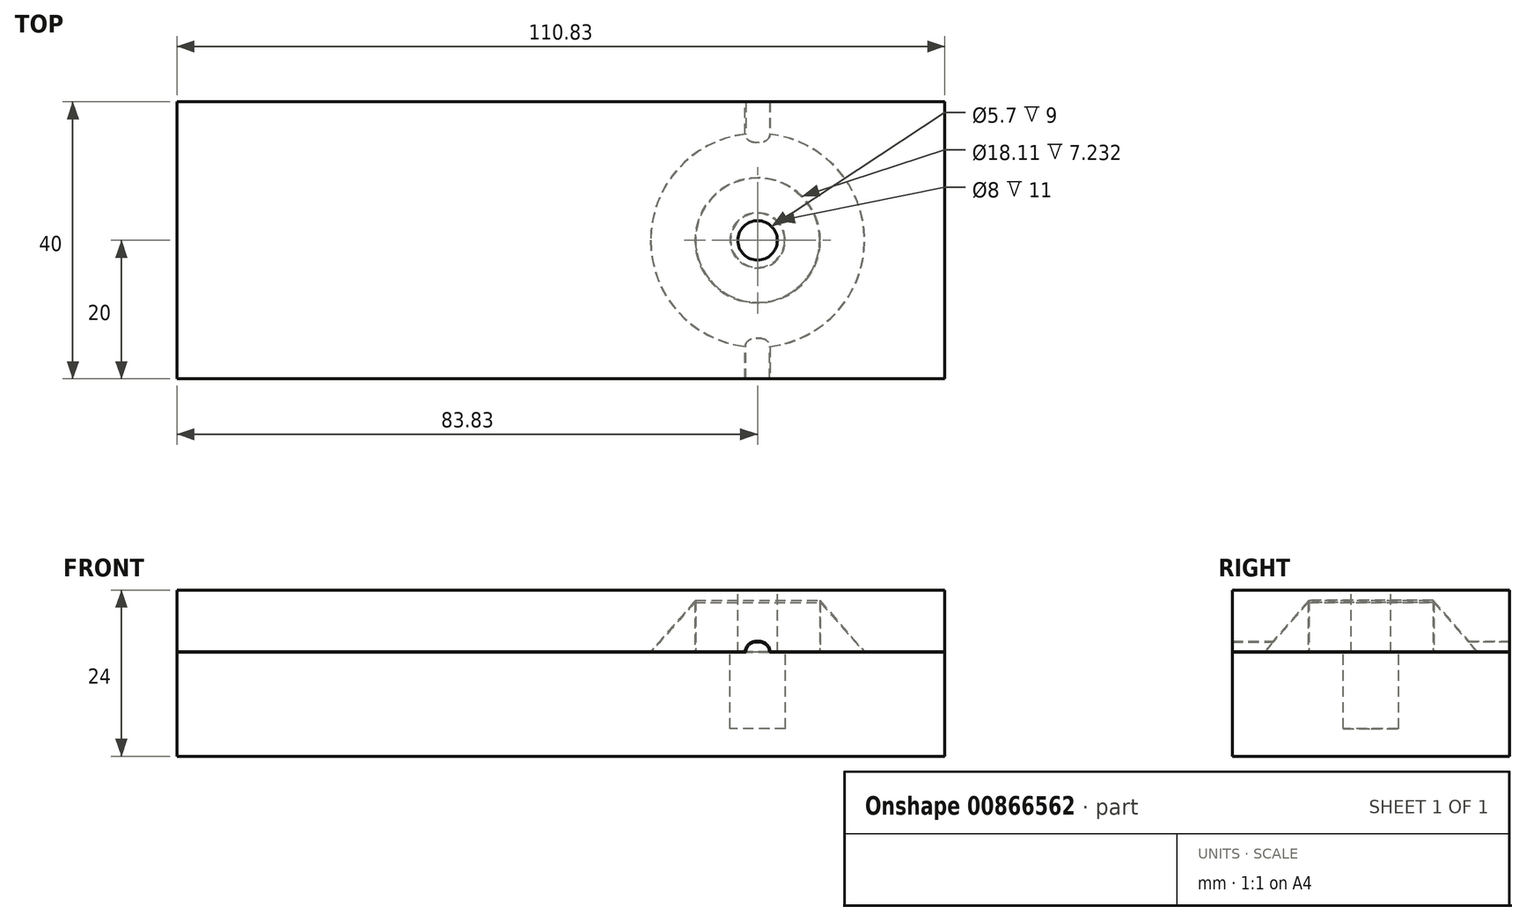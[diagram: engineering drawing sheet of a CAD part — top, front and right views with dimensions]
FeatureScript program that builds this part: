
annotation { "Feature Type Name" : "Feature", "Feature Type Description" : "" }
export const myFeature = defineFeature(function(context is Context, id is Id, definition is map)
    precondition{}
    {
        {
            var Q0;
            Q0=qCreatedBy(makeId("Top.planeOp"),FACE);
            var sketch = newSketch(context, id + "F0", { "sketchPlane" : qUnion([Q0])});
            skLineSegment(sketch, "E0.bottom", {"start": v(27, -20) * mm, "end": v(-83.83, -20) * mm});
            skLineSegment(sketch, "E0.top", {"start": v(27, 20) * mm, "end": v(-83.83, 20) * mm});
            skLineSegment(sketch, "E0.left", {"start": v(27, -20) * mm, "end": v(27, 20) * mm});
            skLineSegment(sketch, "E0.right", {"start": v(-83.83, -20) * mm, "end": v(-83.83, 20) * mm});
            skSolve(sketch);
        }
        {
            var Q0;
            Q0=makeQuery(id+"F0.imprint","IMPRINT",FACE,{"disambiguationData":[TD([[makeQuery(id+"F0.imprint","IMPRINT",EDGE,{"derivedFrom":sQuery(id+"F0.wireOp",EDGE,"E0.bottom")}),-1.0]])]});
            extrude(context, id + "F1", {"entities" : qUnion([Q0]), "depth" : 15 * mm, "offsetDistance" : 25 * mm});
        }
        {
            var Q0;
            Q0=makeQuery(id+"F1.opExtrude","CAP_FACE",FACE,{"disambiguationData":[OSD([sQuery(id+"F0.wireOp",EDGE,"E0.bottom"),sQuery(id+"F0.wireOp",EDGE,"E0.top"),sQuery(id+"F0.wireOp",EDGE,"E0.left"),sQuery(id+"F0.wireOp",EDGE,"E0.right")])],"isStart":false});
            var sketch = newSketch(context, id + "F2", { "sketchPlane" : qUnion([Q0])});
            skCircle(sketch, "E1", {"center": v(0, 0) * mm, "radius": 4 * mm});
            skSolve(sketch);
        }
        {
            var Q0;
            Q0=qCreatedBy(makeId("Right.planeOp"),FACE);
            var sketch = newSketch(context, id + "F3", { "sketchPlane" : qUnion([Q0])});
            skLineSegment(sketch, "E2", {"start": v(9.06, 15) * mm, "end": v(9.06, 22.23) * mm});
            skLineSegment(sketch, "E3", {"start": v(9.06, 22.23) * mm, "end": v(15.4, 15) * mm});
            skLineSegment(sketch, "E4", {"start": v(15.4, 15) * mm, "end": v(9.06, 15) * mm});
            skSolve(sketch);
        }
        {
            var Q0;
            Q0=makeQuery(id+"F3.imprint","IMPRINT",FACE,{"disambiguationData":[TD([[makeQuery(id+"F3.imprint","IMPRINT",EDGE,{"derivedFrom":sQuery(id+"F3.wireOp",EDGE,"E2")}),-1.0]])]});
            var Q1;
            Q1=sQuery(id+"F2.wireOp",EDGE,"E1");
            revolve(context, id + "F4", {"operationType" : NewBodyOperationType.ADD, "surfaceOperationType" : NewSurfaceOperationType.NEW, "entities" : qUnion([Q0]), "axis" : qUnion([Q1]), "revolveType" : RevolveType.FULL});
        }
        {
            var Q0;
            Q0 = qSketchRegion(id + "F2", true);
            extrude(context, id + "F5", {"entities" : qUnion([Q0]), "operationType" : NewBodyOperationType.REMOVE, "oppositeDirection" : true, "depth" : 11 * mm, "offsetDistance" : 25 * mm});
        }
        {
            var Q0;
            {var subQ0=sQuery(id+"F0.wireOp",EDGE,"E0.left");var subQ1=sQuery(id+"F0.wireOp",EDGE,"E0.top");var subQ2=sQuery(id+"F0.wireOp",EDGE,"E0.right");var subQ3=sQuery(id+"F0.wireOp",EDGE,"E0.bottom");Q0=makeQuery(id+"F4.boolean.opBoolean","SPLIT",FACE,{"disambiguationData":[TD([makeQuery(id+"F1.opExtrude","SWEPT_FACE",FACE,{"disambiguationData":[OSD([subQ3])]})])],"derivedFrom":makeQuery(id+"F1.opExtrude","CAP_FACE",FACE,{"disambiguationData":[OSD([subQ3,subQ1,subQ0,subQ2])],"isStart":false})});}
            var sketch = newSketch(context, id + "F6", { "sketchPlane" : qUnion([Q0])});
            skLineSegment(sketch, "E5.bottom", {"start": v(1.71, 20) * mm, "end": v(-1.71, 20) * mm});
            skLineSegment(sketch, "E5.top", {"start": v(1.71, 10.82) * mm, "end": v(-1.71, 10.82) * mm});
            skLineSegment(sketch, "E5.left", {"start": v(1.71, 20) * mm, "end": v(1.71, 10.82) * mm});
            skLineSegment(sketch, "E5.right", {"start": v(-1.71, 20) * mm, "end": v(-1.71, 10.82) * mm});
            skPoint(sketch, "E5.middle", {"position": v(0, 15.41) * mm});
            skLineSegment(sketch, "E6.MirrorCS", {"start": v(-1.71, -20) * mm, "end": v(-1.71, -10.82) * mm});
            skLineSegment(sketch, "E7.MirrorCS", {"start": v(1.71, -20) * mm, "end": v(-1.71, -20) * mm});
            skLineSegment(sketch, "E8.MirrorCS", {"start": v(1.71, -20) * mm, "end": v(1.71, -10.82) * mm});
            skLineSegment(sketch, "E9.MirrorCS", {"start": v(1.71, -10.82) * mm, "end": v(-1.71, -10.82) * mm});
            skSolve(sketch);
        }
        {
            var Q0;
            Q0 = qSketchRegion(id + "F6", true);
            extrude(context, id + "F7", {"entities" : qUnion([Q0]), "operationType" : NewBodyOperationType.ADD, "depth" : 1.5 * mm, "offsetDistance" : 25 * mm});
        }
        {
            var Q0;
            Q0=makeQuery(id+"F7.opExtrude","CAP_EDGE",EDGE,{"disambiguationData":[OSD([sQuery(id+"F6.wireOp",EDGE,"E6.MirrorCS")])],"isStart":false});
            var Q1;
            Q1=makeQuery(id+"F7.opExtrude","CAP_EDGE",EDGE,{"disambiguationData":[OSD([sQuery(id+"F6.wireOp",EDGE,"E8.MirrorCS")])],"isStart":false});
            var Q2;
            Q2=makeQuery(id+"F7.opExtrude","CAP_EDGE",EDGE,{"disambiguationData":[OSD([sQuery(id+"F6.wireOp",EDGE,"E5.right")])],"isStart":false});
            var Q3;
            Q3=makeQuery(id+"F7.opExtrude","CAP_EDGE",EDGE,{"disambiguationData":[OSD([sQuery(id+"F6.wireOp",EDGE,"E5.left")])],"isStart":false});
            fillet(context, id + "F8", {"entities" : qUnion([Q0, Q1, Q2, Q3]), "radius" : 1.5 * mm, "tangentPropagation" : true, "allowEdgeOverflow" : false});
        }
        {
            var Q0;
            Q0=qCreatedBy(makeId("Top.planeOp"),FACE);
            cPlane(context, id + "F9", {"entities" : qUnion([Q0]), "cplaneType" : CPlaneType.OFFSET, "offset" : 15 * mm, "width" : 150 * mm, "height" : 150 * mm});
        }
        {
            var Q0;
            Q0=qCreatedBy(id+"F9.planeOp",FACE);
            var sketch = newSketch(context, id + "F10", { "sketchPlane" : qUnion([Q0])});
            skLineSegment(sketch, "E10.bottom", {"start": v(-83.83, 20) * mm, "end": v(27, 20) * mm});
            skLineSegment(sketch, "E10.top", {"start": v(-83.83, -20) * mm, "end": v(27, -20) * mm});
            skLineSegment(sketch, "E10.left", {"start": v(-83.83, 20) * mm, "end": v(-83.83, -20) * mm});
            skLineSegment(sketch, "E10.right", {"start": v(27, 20) * mm, "end": v(27, -20) * mm});
            skSolve(sketch);
        }
        {
            var Q0;
            Q0 = qSketchRegion(id + "F10", true);
            extrude(context, id + "F11", {"entities" : qUnion([Q0]), "depth" : 9 * mm, "offsetDistance" : 25 * mm});
        }
        {
            var Q0;
            Q0=makeQuery(id+"F1.opExtrude","SWEPT_BODY",BODY,{"disambiguationData":[OSD([sQuery(id+"F0.wireOp",EDGE,"E0.bottom"),sQuery(id+"F0.wireOp",EDGE,"E0.top"),sQuery(id+"F0.wireOp",EDGE,"E0.left"),sQuery(id+"F0.wireOp",EDGE,"E0.right")])]});
            var Q1;
            Q1=makeQuery(id+"F11.opExtrude","SWEPT_BODY",BODY,{"disambiguationData":[OSD([sQuery(id+"F10.wireOp",EDGE,"E10.bottom"),sQuery(id+"F10.wireOp",EDGE,"E10.top"),sQuery(id+"F10.wireOp",EDGE,"E10.left"),sQuery(id+"F10.wireOp",EDGE,"E10.right")])]});
            booleanBodies(context, id + "F12", {"operationType" : BooleanOperationType.SUBTRACTION, "tools" : qUnion([Q0]), "targets" : qUnion([Q1]), "offset" : true, "offsetAll" : true, "offsetDistance" : 0.1 * mm, "keepTools" : true});
        }
        {
            var Q0;
            Q0=makeQuery(id+"F11.opExtrude","CAP_FACE",FACE,{"disambiguationData":[OSD([sQuery(id+"F10.wireOp",EDGE,"E10.bottom"),sQuery(id+"F10.wireOp",EDGE,"E10.top"),sQuery(id+"F10.wireOp",EDGE,"E10.left"),sQuery(id+"F10.wireOp",EDGE,"E10.right")])],"isStart":false});
            var sketch = newSketch(context, id + "F13", { "sketchPlane" : qUnion([Q0])});
            skCircle(sketch, "E11", {"center": v(0, 0) * mm, "radius": 2.85 * mm});
            skSolve(sketch);
        }
        {
            var Q0;
            Q0 = qSketchRegion(id + "F13", true);
            extrude(context, id + "F14", {"entities" : qUnion([Q0]), "operationType" : NewBodyOperationType.REMOVE, "endBound" : BoundingType.UP_TO_NEXT, "oppositeDirection" : true, "depth" : 25 * mm, "offsetDistance" : 25 * mm});
        }
    });
